# Revit family: CLS
name_source: partatom
category: Pipe Accessories
revit_build: Autodesk Revit 2013 (Build: 20120221_2030(x64)
units: mm (PartAtom-declared; Revit-internal decimal feet)

## types (8) — shared parameters
Description = Piston Operated Water Hammer Arrestor With SWT Connection
Manufacturer = Mifab
Model = CLS
URL = www.mifab.com

## per-type parameters (varying)
| type | Diameter | Length | Material | SWT Connection |
| AA | 0' - 0 7/8" | 0' - 6 1/2" | Copper | 0' - 0 1/2" |
| AA- | 0' - 0 7/8" | 0' - 6 1/2" | Metal-Watts-Copper | 0' - 0 3/4" |
| A | 0' - 1 1/8" | 0' - 8 1/4" | Metal-Watts-Copper | 0' - 0 1/2" |
| B | 0' - 1 1/8" | 0' - 10" | Metal-Watts-Copper | 0' - 0 3/4" |
| C | 0' - 1 3/8" | 1' - 0 1/2" | Metal-Watts-Copper | 0' - 1" |
| D | 0' - 2 1/8" | 0' - 11" | Metal-Watts-Copper | 0' - 1" |
| E | 0' - 2 1/8" | 1' - 1 1/2" | Metal-Watts-Copper | 0' - 1" |
| F | 0' - 2 1/8" | 1' - 4" | Metal-Watts-Copper | 0' - 1" |

## geometry (parser evidence)
native form markers: Blend x4, Sweep x1
no freeform markers — native parametric forms only
